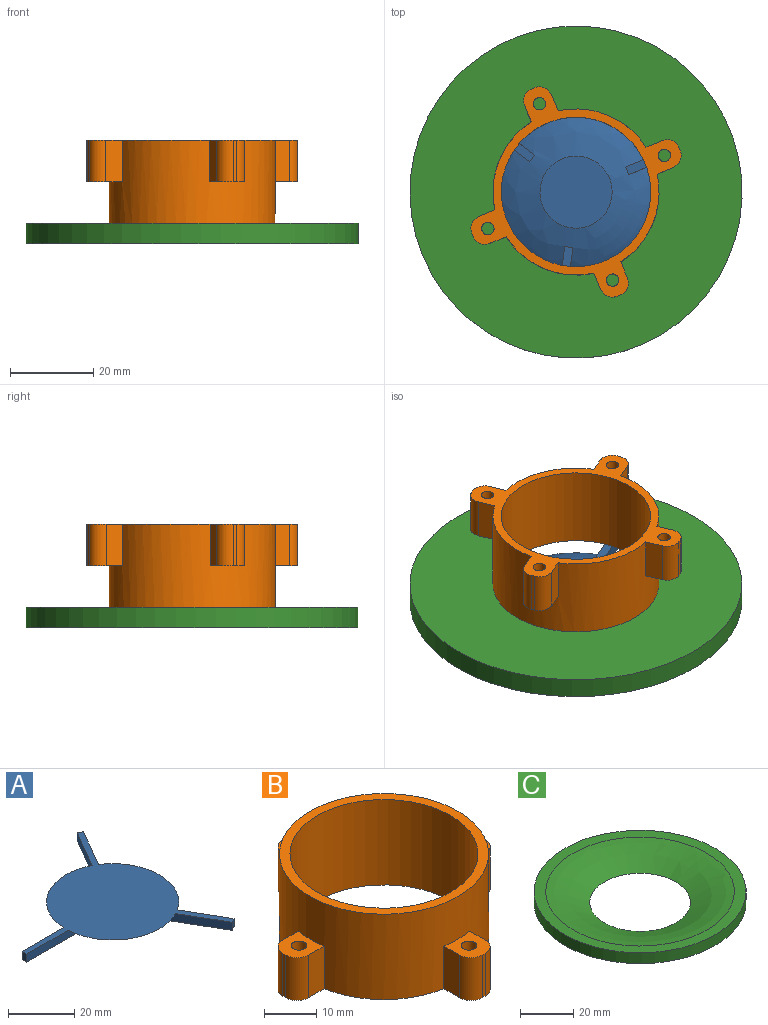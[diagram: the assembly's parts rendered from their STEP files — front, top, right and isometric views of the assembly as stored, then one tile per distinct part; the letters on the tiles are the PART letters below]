
ASSEMBLY  parts=3 mates=4
PART A: 15 faces, bbox 57.8x66.4x4 mm
  f0: bspline ~39.98x39.98mm, area 1058.9mm2, adj f1,f2,f3,f5,f6,f8,f9,f10
  f1: plane 66.41x57.78mm, normal (0,0,1), area 1363.6mm2, adj f0,f3,f4,f5,f7,f8,f9,f11
  f2: plane 17.39x17.39mm, normal (0,0,-1), area 237.1mm2, adj f0
  f3: plane 24.42x3mm, normal (0,1,0), area 62mm2, adj f0,f1,f4,f6
  f4: plane 3x2mm, normal (-1,0,0), area 6mm2, adj f1,f3,f5,f6
  f5: plane 24.42x3mm, normal (0,-1,0), area 62mm2, adj f0,f1,f4,f6
  f6: plane 24.42x2mm, normal (0,0,-1), area 48.8mm2, adj f0,f3,f4,f5
  f7: plane 3x1.73mm, normal (0.5,-0.87,0), area 6mm2, adj f1,f8,f9,f10
  f8: plane 21.15x12.21mm, normal (0.87,0.5,0), area 62mm2, adj f0,f1,f7,f10
  f9: plane 21.14x12.21mm, normal (-0.87,-0.5,0), area 62mm2, adj f0,f1,f7,f10
  f10: plane 22.15x13.94mm, normal (0,0,-1), area 48.8mm2, adj f0,f7,f8,f9
  f11: plane 3x1.73mm, normal (0.5,0.87,0), area 6mm2, adj f1,f12,f13,f14
  f12: plane 21.14x12.21mm, normal (-0.87,0.5,0), area 62mm2, adj f0,f1,f11,f14
  f13: plane 21.15x12.21mm, normal (0.87,-0.5,0), area 62mm2, adj f0,f1,f11,f14
  f14: plane 22.15x13.94mm, normal (0,0,-1), area 48.8mm2, adj f0,f11,f12,f13
PART B: 32 faces, bbox 54x54x20 mm
  f0: cylinder r=20mm len=40mm, axis (0,0,-1), area 2231.8mm2, adj f1,f2,f5,f6,f7,f8,f10,f11
  f1: plane 40x40mm, normal (0,0,1), area 238.8mm2, adj f0,f3
  f2: plane 54x54mm, normal (0,0,-1), area 392.9mm2, adj f0,f3,f4,f5,f6,f8,f9,f10
  f3: cylinder r=18mm len=36mm, axis (0,0,-1), area 2261.9mm2, adj f1,f2
  f4: plane 10x0.8mm, normal (0,1,0), area 8mm2, adj f2,f7,f24,f25
  f5: plane 10x4.21mm, normal (-1,0,0), area 42.1mm2, adj f0,f2,f7,f24
  f6: plane 10x4.21mm, normal (1,0,0), area 42.1mm2, adj f0,f2,f7,f25
  f7: plane 7.31x7mm, normal (0,0,1), area 38.5mm2, adj f0,f4,f5,f6,f24,f25,f31
  f8: plane 10x4.21mm, normal (0,1,0), area 42.1mm2, adj f0,f2,f11,f27
  f9: plane 10x0.8mm, normal (-1,0,0), area 8mm2, adj f2,f11,f26,f27
  f10: plane 10x4.21mm, normal (0,-1,0), area 42.1mm2, adj f0,f2,f11,f26
  f11: plane 7.31x7mm, normal (0,0,1), area 38.5mm2, adj f0,f8,f9,f10,f26,f27,f30
  f12: plane 10x0.8mm, normal (0,-1,0), area 8mm2, adj f2,f15,f20,f21
  f13: plane 10x4.21mm, normal (1,0,0), area 42.1mm2, adj f0,f2,f15,f21
  f14: plane 10x4.21mm, normal (-1,0,0), area 42.1mm2, adj f0,f2,f15,f20
  f15: plane 7.31x7mm, normal (0,0,1), area 38.5mm2, adj f0,f12,f13,f14,f20,f21,f29
  f16: plane 10x0.8mm, normal (1,0,0), area 8mm2, adj f2,f19,f22,f23
  f17: plane 10x4.21mm, normal (0,1,0), area 42.1mm2, adj f0,f2,f19,f23
  f18: plane 10x4.21mm, normal (0,-1,0), area 42.1mm2, adj f0,f2,f19,f22
  f19: plane 7.31x7mm, normal (0,0,1), area 38.5mm2, adj f0,f16,f17,f18,f22,f23,f28
  f20: cylinder r=3.1mm len=10mm, axis (0,0,1), area 48.7mm2, adj f2,f12,f14,f15
  f21: cylinder r=3.1mm len=10mm, axis (0,0,-1), area 48.7mm2, adj f2,f12,f13,f15
  f22: cylinder r=3.1mm len=10mm, axis (0,0,1), area 48.7mm2, adj f2,f16,f18,f19
  f23: cylinder r=3.1mm len=10mm, axis (0,0,-1), area 48.7mm2, adj f2,f16,f17,f19
  f24: cylinder r=3.1mm len=10mm, axis (0,0,-1), area 48.7mm2, adj f2,f4,f5,f7
  f25: cylinder r=3.1mm len=10mm, axis (0,0,1), area 48.7mm2, adj f2,f4,f6,f7
  f26: cylinder r=3.1mm len=10mm, axis (0,0,-1), area 48.7mm2, adj f2,f9,f10,f11
  f27: cylinder r=3.1mm len=10mm, axis (0,0,1), area 48.7mm2, adj f2,f8,f9,f11
  f28: cylinder r=1.5mm len=10mm, axis (0,0,-1), area 94.2mm2, adj f2,f19
  f29: cylinder r=1.5mm len=10mm, axis (0,0,-1), area 94.2mm2, adj f2,f15
  f30: cylinder r=1.5mm len=10mm, axis (0,0,-1), area 94.2mm2, adj f2,f11
  f31: cylinder r=1.5mm len=10mm, axis (0,0,-1), area 94.2mm2, adj f2,f7
PART C: 4 faces, bbox 80x80x5 mm
  f0: cylinder r=40mm len=80mm, axis (0,0,-1), area 1256.6mm2, adj f1,f2
  f1: plane 80.01x80.01mm, normal (0,0,1), area 1049.4mm2, adj f0,f3
  f2: plane 80.02x80.02mm, normal (0,0,-1), area 3892.6mm2, adj f0,f3
  f3: bspline ~71.17x71.17mm, area 2971.8mm2, adj f1,f2
PLACE A rot(axis=(0.2,-0.98,0),180deg) t=(35.72,12.33,60)mm
PLACE B rot(axis=(0.2,-0.98,0),180deg) t=(35.72,12.33,81)mm
PLACE C rot(axis=(0.2,-0.98,0),180deg) t=(35.72,12.33,61)mm
MATE cylindrical C.f0 <-> A.f2  axis (0,0,1) through (35.72,12.33,61)mm
MATE cylindrical A.f2 <-> B.f0  axis (0,0,1) through (35.72,12.33,60)mm
MATE planar A.f1 <-> C.f1  axis (0,0,-1) through (35.72,12.33,56)mm
MATE planar C.f0 <-> B.f0  axis (0,0,1) through (35.72,12.33,61)mm
